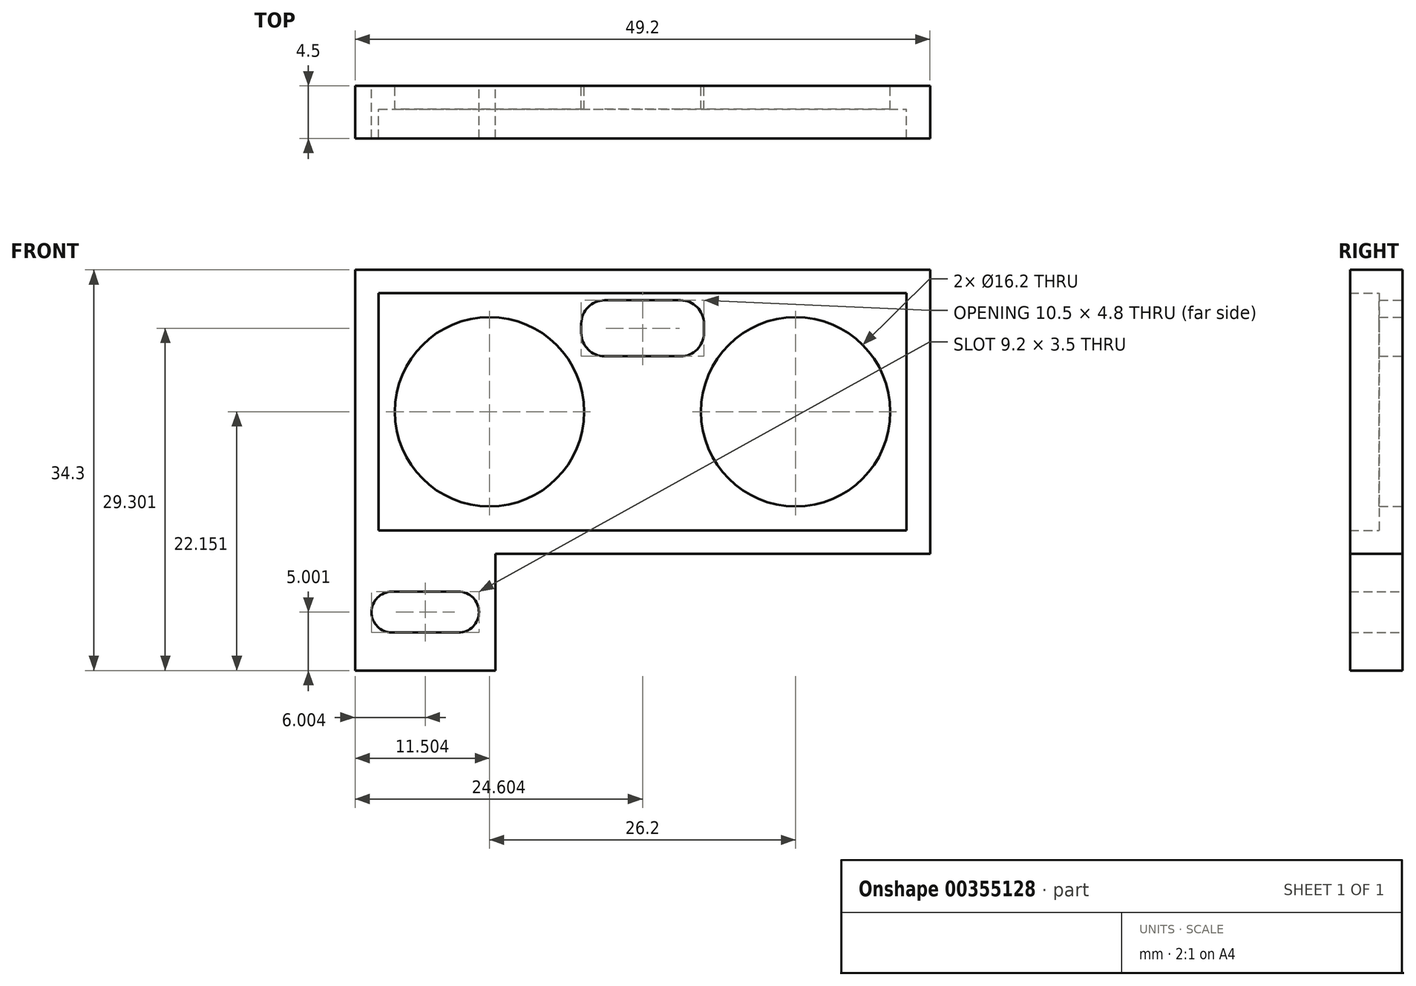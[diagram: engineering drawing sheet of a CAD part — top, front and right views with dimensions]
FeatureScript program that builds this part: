
annotation { "Feature Type Name" : "Feature", "Feature Type Description" : "" }
export const myFeature = defineFeature(function(context is Context, id is Id, definition is map)
    precondition{}
    {
        {
            var Q0;
            Q0=qCreatedBy(makeId("Front.planeOp"),FACE);
            var sketch = newSketch(context, id + "F0", { "sketchPlane" : qUnion([Q0])});
            skLineSegment(sketch, "E0.bottom", {"start": v(-22.23, 13.22) * mm, "end": v(22.97, 13.22) * mm});
            skLineSegment(sketch, "E0.top", {"start": v(-22.23, -7.08) * mm, "end": v(22.97, -7.08) * mm});
            skLineSegment(sketch, "E0.left", {"start": v(-22.23, 13.22) * mm, "end": v(-22.23, -7.08) * mm});
            skLineSegment(sketch, "E0.right", {"start": v(22.97, 13.22) * mm, "end": v(22.97, -7.08) * mm});
            skLineSegment(sketch, "E1", {"start": v(0.37, 13.22) * mm, "end": v(0.37, -7.08) * mm, "construction": true});
            skCircle(sketch, "E2", {"center": v(-12.73, 3.07) * mm, "radius": 8.1 * mm});
            skPoint(sketch, "E3", {"position": v(-22.23, 3.07) * mm});
            skCircle(sketch, "E4.MirrorC", {"center": v(13.47, 3.07) * mm, "radius": 8.1 * mm});
            skLineSegment(sketch, "E5.0", {"start": v(-24.23, 15.22) * mm, "end": v(24.97, 15.22) * mm});
            skLineSegment(sketch, "E5.1", {"start": v(-24.23, 15.22) * mm, "end": v(-24.23, -9.08) * mm});
            skLineSegment(sketch, "E5.2", {"start": v(-24.23, -9.08) * mm, "end": v(24.97, -9.08) * mm});
            skLineSegment(sketch, "E5.3", {"start": v(24.97, 15.22) * mm, "end": v(24.97, -9.08) * mm});
            skLineSegment(sketch, "E6.bottom", {"start": v(5.62, 12.62) * mm, "end": v(-4.88, 12.62) * mm});
            skLineSegment(sketch, "E6.top", {"start": v(5.62, 7.82) * mm, "end": v(-4.88, 7.82) * mm});
            skLineSegment(sketch, "E6.left", {"start": v(5.62, 12.62) * mm, "end": v(5.62, 7.82) * mm});
            skLineSegment(sketch, "E6.right", {"start": v(-4.88, 12.62) * mm, "end": v(-4.88, 7.82) * mm});
            skPoint(sketch, "E6.middle", {"position": v(0.37, 10.22) * mm});
            skLineSegment(sketch, "E7", {"start": v(-24.23, 3.07) * mm, "end": v(24.97, 3.07) * mm, "construction": true});
            skLineSegment(sketch, "E8.MirrorCS", {"start": v(18.97, -19.08) * mm, "end": v(18.97, -9.08) * mm, "construction": true});
            skLineSegment(sketch, "E9.MirrorCS", {"start": v(24.97, -9.08) * mm, "end": v(12.97, -9.08) * mm});
            skLineSegment(sketch, "E10.MirrorCS", {"start": v(-12.23, -9.08) * mm, "end": v(-12.23, -19.08) * mm});
            skLineSegment(sketch, "E11.MirrorCS", {"start": v(-24.23, -19.08) * mm, "end": v(-12.23, -19.08) * mm});
            skLineSegment(sketch, "E12.MirrorCS", {"start": v(-15.38, -12.33) * mm, "end": v(-21.08, -12.33) * mm});
            skPoint(sketch, "E13.MirrorP", {"position": v(24.97, -14.08) * mm});
            skLineSegment(sketch, "E14.MirrorCS", {"start": v(24.97, -19.08) * mm, "end": v(12.97, -19.08) * mm});
            skLineSegment(sketch, "E15.MirrorCS", {"start": v(-15.38, -15.83) * mm, "end": v(-21.08, -15.83) * mm});
            skLineSegment(sketch, "E16.MirrorCS", {"start": v(-24.23, -9.08) * mm, "end": v(-24.23, -19.08) * mm});
            skCircle(sketch, "E17.MirrorC", {"center": v(-15.38, -14.08) * mm, "radius": 1.75 * mm});
            skPoint(sketch, "E18.MirrorP", {"position": v(-24.23, -14.08) * mm});
            skLineSegment(sketch, "E19.MirrorCS", {"start": v(24.97, -9.08) * mm, "end": v(24.97, -19.08) * mm});
            skLineSegment(sketch, "E20.MirrorCS", {"start": v(-24.23, -9.08) * mm, "end": v(-12.23, -9.08) * mm});
            skLineSegment(sketch, "E21.MirrorCS", {"start": v(12.97, -9.08) * mm, "end": v(12.97, -19.08) * mm});
            skCircle(sketch, "E22.MirrorC", {"center": v(-21.08, -14.08) * mm, "radius": 1.75 * mm});
            skCircle(sketch, "E23.MirrorC", {"center": v(16.12, -14.08) * mm, "radius": 1.75 * mm});
            skCircle(sketch, "E24.MirrorC", {"center": v(21.82, -14.08) * mm, "radius": 1.75 * mm});
            skLineSegment(sketch, "E25.MirrorCS", {"start": v(16.12, -15.83) * mm, "end": v(21.82, -15.83) * mm});
            skLineSegment(sketch, "E26.MirrorCS", {"start": v(16.12, -12.33) * mm, "end": v(21.82, -12.33) * mm});
            skSolve(sketch);
        }
        {
            var Q0;
            Q0=makeQuery(id+"F0.imprint","IMPRINT",FACE,{"disambiguationData":[TD([[makeQuery(id+"F0.imprint","IMPRINT",EDGE,{"derivedFrom":sQuery(id+"F0.wireOp",EDGE,"E0.bottom")}),-1.0]])]});
            extrude(context, id + "F1", {"entities" : qUnion([Q0]), "depth" : 2 * mm});
        }
        {
            var Q0;
            Q0=makeQuery(id+"F0.imprint","IMPRINT",FACE,{"disambiguationData":[TD([[makeQuery(id+"F0.imprint","IMPRINT",EDGE,{"derivedFrom":sQuery(id+"F0.wireOp",EDGE,"E0.bottom")}),1.0]])]});
            var Q1;
            Q1=makeQuery(id+"F0.imprint","IMPRINT",FACE,{"disambiguationData":[TD([[makeQuery(id+"F0.imprint","IMPRINT",EDGE,{"derivedFrom":sQuery(id+"F0.wireOp",EDGE,"41134aa3-82a6-44f2-9138-f71fa3e3d42e0.MirrorCS")}),-1.0]])]});
            var Q2;
            Q2=makeQuery(id+"F0.imprint","IMPRINT",FACE,{"disambiguationData":[TD([[makeQuery(id+"F0.imprint","IMPRINT",EDGE,{"derivedFrom":sQuery(id+"F0.wireOp",EDGE,"ZdMusW5R-1aZ7-cEhM-uIft-sHiM9ahLCE1K.bottom")}),-1.0]])]});
            var Q3;
            Q3=makeQuery(id+"F0.imprint","IMPRINT",FACE,{"disambiguationData":[TD([[makeQuery(id+"F0.imprint","IMPRINT",EDGE,{"derivedFrom":sQuery(id+"F0.wireOp",EDGE,"E10.MirrorCS")}),-1.0]])]});
            var Q4;
            Q4=makeQuery(id+"F0.imprint","IMPRINT",FACE,{"disambiguationData":[TD([[makeQuery(id+"F0.imprint","IMPRINT",EDGE,{"derivedFrom":sQuery(id+"F0.wireOp",EDGE,"E9.MirrorCS")}),1.0]])]});
            extrude(context, id + "F2", {"entities" : qUnion([Q0, Q1, Q2, Q3, Q4]), "operationType" : NewBodyOperationType.ADD, "depth" : 4.5 * mm});
        }
        {
            var Q0;
            Q0=makeQuery(id+"F1.opExtrude","SWEPT_EDGE",EDGE,{"disambiguationData":[OSD([sQuery(id+"F0.wireOp",EDGE,"E6.top"),sQuery(id+"F0.wireOp",EDGE,"E6.right")])]});
            var Q1;
            Q1=makeQuery(id+"F1.opExtrude","SWEPT_EDGE",EDGE,{"disambiguationData":[OSD([sQuery(id+"F0.wireOp",EDGE,"E6.bottom"),sQuery(id+"F0.wireOp",EDGE,"E6.right")])]});
            var Q2;
            Q2=makeQuery(id+"F1.opExtrude","SWEPT_EDGE",EDGE,{"disambiguationData":[OSD([sQuery(id+"F0.wireOp",EDGE,"E6.bottom"),sQuery(id+"F0.wireOp",EDGE,"E6.left")])]});
            var Q3;
            Q3=makeQuery(id+"F1.opExtrude","SWEPT_EDGE",EDGE,{"disambiguationData":[OSD([sQuery(id+"F0.wireOp",EDGE,"E6.top"),sQuery(id+"F0.wireOp",EDGE,"E6.left")])]});
            fillet(context, id + "F3", {"entities" : qUnion([Q0, Q1, Q2, Q3]), "radius" : 2 * mm, "tangentPropagation" : true, "allowEdgeOverflow" : false});
        }
    });
